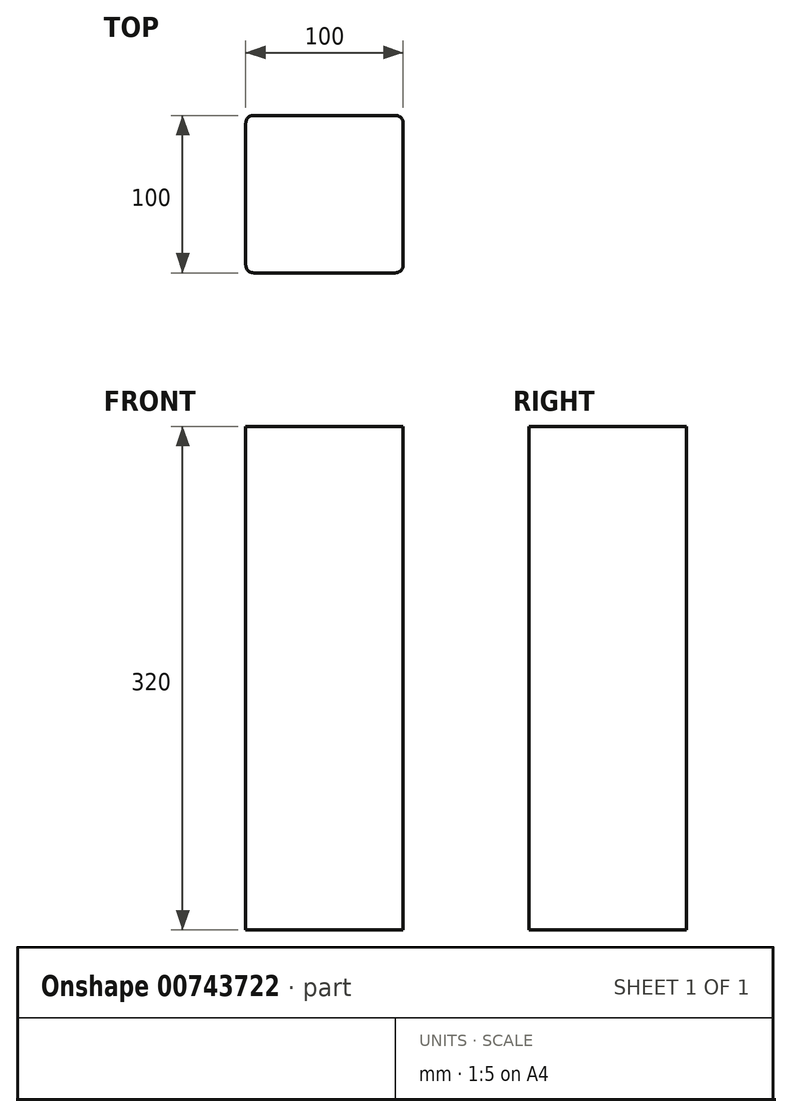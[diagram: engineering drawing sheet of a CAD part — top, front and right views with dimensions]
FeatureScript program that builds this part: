
annotation { "Feature Type Name" : "Feature", "Feature Type Description" : "" }
export const myFeature = defineFeature(function(context is Context, id is Id, definition is map)
    precondition{}
    {
        {
            var Q0;
            Q0=qCreatedBy(makeId("Top.planeOp"),FACE);
            var sketch = newSketch(context, id + "F0", { "sketchPlane" : qUnion([Q0])});
            skLineSegment(sketch, "E0.bottom", {"start": v(45, -50) * mm, "end": v(-45, -50) * mm});
            skLineSegment(sketch, "E0.top", {"start": v(45, 50) * mm, "end": v(-45, 50) * mm});
            skLineSegment(sketch, "E0.left", {"start": v(50, -45) * mm, "end": v(50, 45) * mm});
            skLineSegment(sketch, "E0.right", {"start": v(-50, -45) * mm, "end": v(-50, 45) * mm});
            skPoint(sketch, "E0.middle", {"position": v(0, 0) * mm});
            skPoint(sketch, "E1.visualSharp", {"position": v(-50, 50) * mm});
            skArc(sketch, "E1.filletArc", {"start": v(-45, 50) * mm, "mid": v(-48.54, 48.54) * mm, "end": v(-50, 45) * mm});
            skPoint(sketch, "E2.visualSharp", {"position": v(50, -50) * mm});
            skArc(sketch, "E2.filletArc", {"start": v(45, -50) * mm, "mid": v(48.54, -48.54) * mm, "end": v(50, -45) * mm});
            skPoint(sketch, "E3.visualSharp", {"position": v(50, 50) * mm});
            skArc(sketch, "E3.filletArc", {"start": v(50, 45) * mm, "mid": v(48.54, 48.54) * mm, "end": v(45, 50) * mm});
            skPoint(sketch, "E4.visualSharp", {"position": v(-50, -50) * mm});
            skArc(sketch, "E4.filletArc", {"start": v(-50, -45) * mm, "mid": v(-48.54, -48.54) * mm, "end": v(-45, -50) * mm});
            skSolve(sketch);
        }
        {
            var Q0;
            Q0=makeQuery(id+"F0.imprint","IMPRINT",FACE,{"disambiguationData":[TD([[makeQuery(id+"F0.imprint","IMPRINT",EDGE,{"derivedFrom":sQuery(id+"F0.wireOp",EDGE,"E0.bottom")}),-1.0]])]});
            extrude(context, id + "F1", {"entities" : qUnion([Q0]), "depth" : 320 * mm, "offsetDistance" : 25 * mm});
        }
    });
